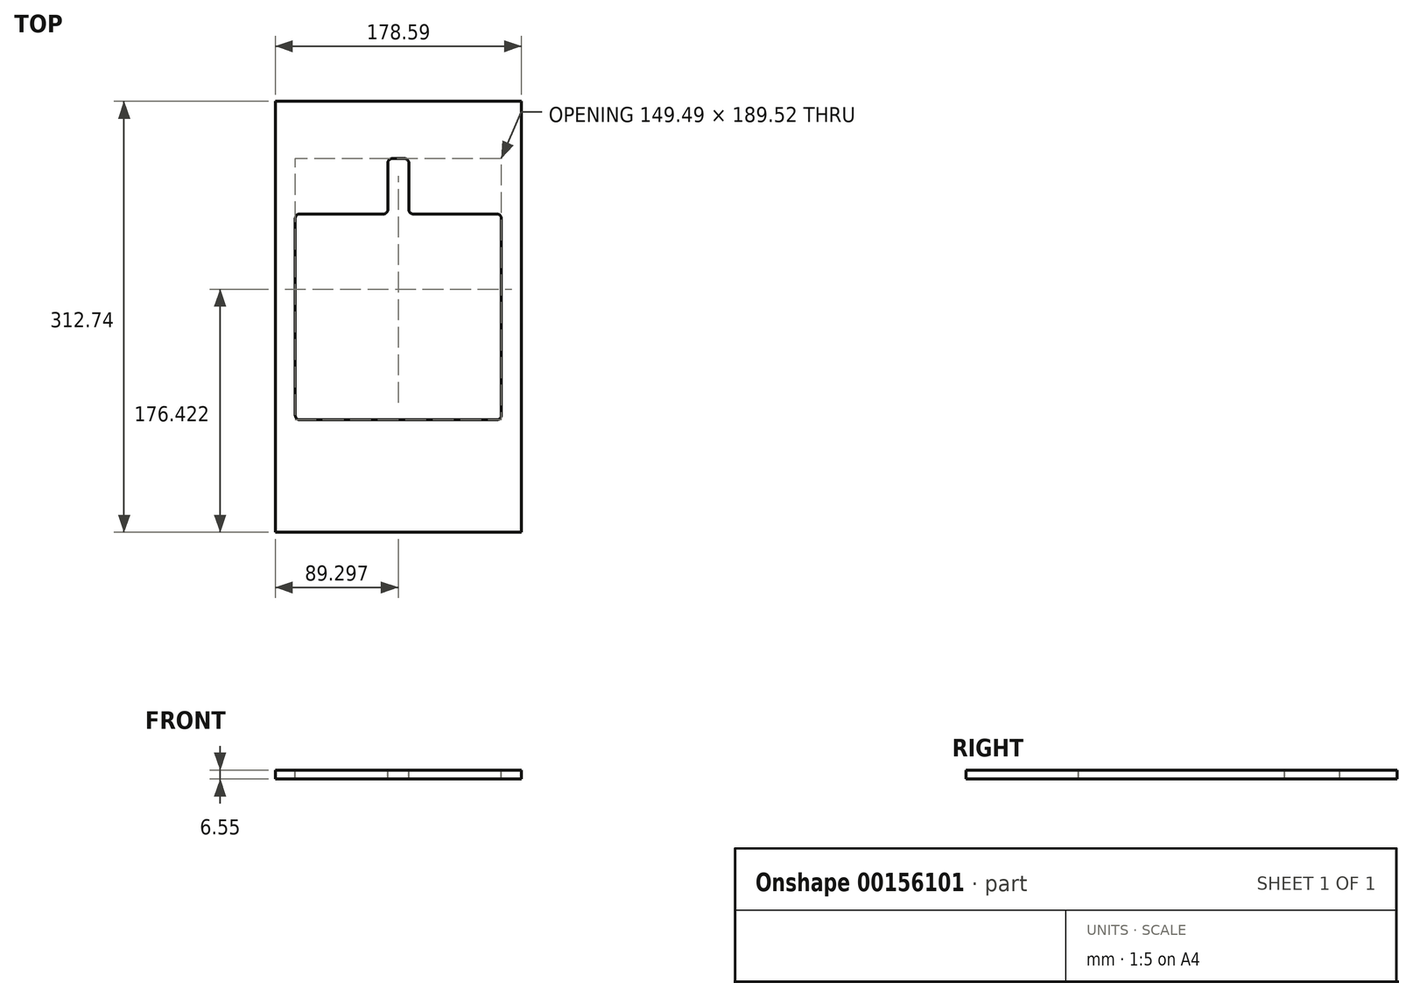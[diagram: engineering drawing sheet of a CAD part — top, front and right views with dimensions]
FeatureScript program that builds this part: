
annotation { "Feature Type Name" : "Feature", "Feature Type Description" : "" }
export const myFeature = defineFeature(function(context is Context, id is Id, definition is map)
    precondition{}
    {
        {
            var Q0;
            Q0=qCreatedBy(makeId("Top.planeOp"),FACE);
            var sketch = newSketch(context, id + "F0", { "sketchPlane" : qUnion([Q0])});
            skLineSegment(sketch, "E0.bottom", {"start": v(0, 0) * mm, "end": v(178.6, 0) * mm});
            skLineSegment(sketch, "E0.top", {"start": v(0, 312.74) * mm, "end": v(178.6, 312.74) * mm});
            skLineSegment(sketch, "E0.left", {"start": v(0, 0) * mm, "end": v(0, 312.74) * mm});
            skLineSegment(sketch, "E0.right", {"start": v(178.6, 0) * mm, "end": v(178.6, 312.74) * mm});
            skSolve(sketch);
        }
        {
            var Q0;
            Q0 = qSketchRegion(id + "F0", true);
            extrude(context, id + "F1", {"entities" : qUnion([Q0]), "depth" : 6.55 * mm});
        }
        {
            var Q0;
            Q0=makeQuery(id+"F1.opExtrude","CAP_FACE",FACE,{"disambiguationData":[OSD([sQuery(id+"F0.wireOp",EDGE,"E0.bottom"),sQuery(id+"F0.wireOp",EDGE,"E0.top"),sQuery(id+"F0.wireOp",EDGE,"E0.left"),sQuery(id+"F0.wireOp",EDGE,"E0.right")])],"isStart":false});
            var sketch = newSketch(context, id + "F2", { "sketchPlane" : qUnion([Q0])});
            skLineSegment(sketch, "E1.bottom", {"start": v(17.73, 231.05) * mm, "end": v(78.5, 231.05) * mm});
            skLineSegment(sketch, "E1.top", {"start": v(17.73, 81.66) * mm, "end": v(160.86, 81.66) * mm});
            skLineSegment(sketch, "E1.left", {"start": v(14.55, 227.88) * mm, "end": v(14.55, 84.84) * mm});
            skLineSegment(sketch, "E1.right", {"start": v(164.04, 227.88) * mm, "end": v(164.04, 84.84) * mm});
            skLineSegment(sketch, "E2", {"start": v(89.3, 312.74) * mm, "end": v(89.3, 0) * mm, "construction": true});
            skLineSegment(sketch, "E3", {"start": v(81.68, 234.23) * mm, "end": v(81.68, 268) * mm});
            skLineSegment(sketch, "E4", {"start": v(96.92, 234.23) * mm, "end": v(96.92, 268) * mm});
            skLineSegment(sketch, "E5", {"start": v(84.85, 271.18) * mm, "end": v(93.74, 271.18) * mm});
            skLineSegment(sketch, "E6.trimOffspring", {"start": v(100.1, 231.05) * mm, "end": v(160.86, 231.05) * mm});
            skPoint(sketch, "E7.visualSharp", {"position": v(14.55, 231.05) * mm});
            skArc(sketch, "E7.filletArc", {"start": v(17.73, 231.05) * mm, "mid": v(15.48, 230.12) * mm, "end": v(14.55, 227.88) * mm});
            skPoint(sketch, "E8.visualSharp", {"position": v(14.55, 81.66) * mm});
            skArc(sketch, "E8.filletArc", {"start": v(14.55, 84.84) * mm, "mid": v(15.48, 82.6) * mm, "end": v(17.73, 81.66) * mm});
            skPoint(sketch, "E9.visualSharp", {"position": v(164.04, 81.66) * mm});
            skArc(sketch, "E9.filletArc", {"start": v(160.86, 81.66) * mm, "mid": v(163.1, 82.6) * mm, "end": v(164.04, 84.84) * mm});
            skPoint(sketch, "E10.visualSharp", {"position": v(164.04, 231.05) * mm});
            skArc(sketch, "E10.filletArc", {"start": v(164.04, 227.88) * mm, "mid": v(163.1, 230.12) * mm, "end": v(160.86, 231.05) * mm});
            skPoint(sketch, "E11.visualSharp", {"position": v(96.92, 231.05) * mm});
            skArc(sketch, "E11.filletArc", {"start": v(96.92, 234.23) * mm, "mid": v(97.85, 231.98) * mm, "end": v(100.1, 231.05) * mm});
            skPoint(sketch, "E12.visualSharp", {"position": v(96.92, 271.18) * mm});
            skArc(sketch, "E12.filletArc", {"start": v(96.92, 268) * mm, "mid": v(95.99, 270.25) * mm, "end": v(93.74, 271.18) * mm});
            skPoint(sketch, "E13.visualSharp", {"position": v(81.68, 271.18) * mm});
            skArc(sketch, "E13.filletArc", {"start": v(84.85, 271.18) * mm, "mid": v(82.6, 270.25) * mm, "end": v(81.68, 268) * mm});
            skPoint(sketch, "E14.visualSharp", {"position": v(81.68, 231.05) * mm});
            skArc(sketch, "E14.filletArc", {"start": v(78.5, 231.05) * mm, "mid": v(80.75, 231.98) * mm, "end": v(81.68, 234.23) * mm});
            skSolve(sketch);
        }
        {
            var Q0;
            Q0=makeQuery(id+"F2.imprint","IMPRINT",FACE,{"disambiguationData":[TD([[makeQuery(id+"F2.imprint","IMPRINT",EDGE,{"derivedFrom":sQuery(id+"F2.wireOp",EDGE,"E1.bottom")}),-1.0]])]});
            extrude(context, id + "F3", {"entities" : qUnion([Q0]), "operationType" : NewBodyOperationType.REMOVE, "oppositeDirection" : true, "depth" : 25.4 * mm});
        }
    });
